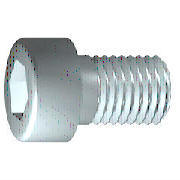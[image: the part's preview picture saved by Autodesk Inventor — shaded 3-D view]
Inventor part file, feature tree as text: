
AUTODESK INVENTOR PART (.ipt)
format: ipt  version: 2022.1 (Build 261234000, 234)  size: 187,904 bytes
history: native  units: mm (DEFAULTED — no unit token found)
features: sketch x2, other x1, extrude x1, plane x1, fillet x1
ambient origin geometry x7: Origin, YZ Plane, XY Plane, X Axis, Y Axis, Z Axis, Center Point
bodies: Solid1 (feature_tree)
feature tree (6):
  other  "Cuerpo"
  extrude  "Ranura"  Depth=2.0mm
  plane  "Work Plane1"
  fillet  "Fillet2"  Radius=2.0mm
  sketch  "Boceto1"  dims[d1=15.0mm d2=0.24548mm d3=2.0mm]
  sketch  "Boceto2"  dims[d4=1.0mm d5=60.0deg d6=2.0mm d7=2.0mm d8=1.732051mm d9=3.8mm d10=90.0deg d11=10.0mm d12=0.0mm d13=15.0mm d14=0.0mm d15=0.24538mm d16=0.24538mm d17=0.2mm d19=0.0mm d26=16.0mm d27=45.0deg d28=0.0mm d29=0.0mm d30=0.1mm]
